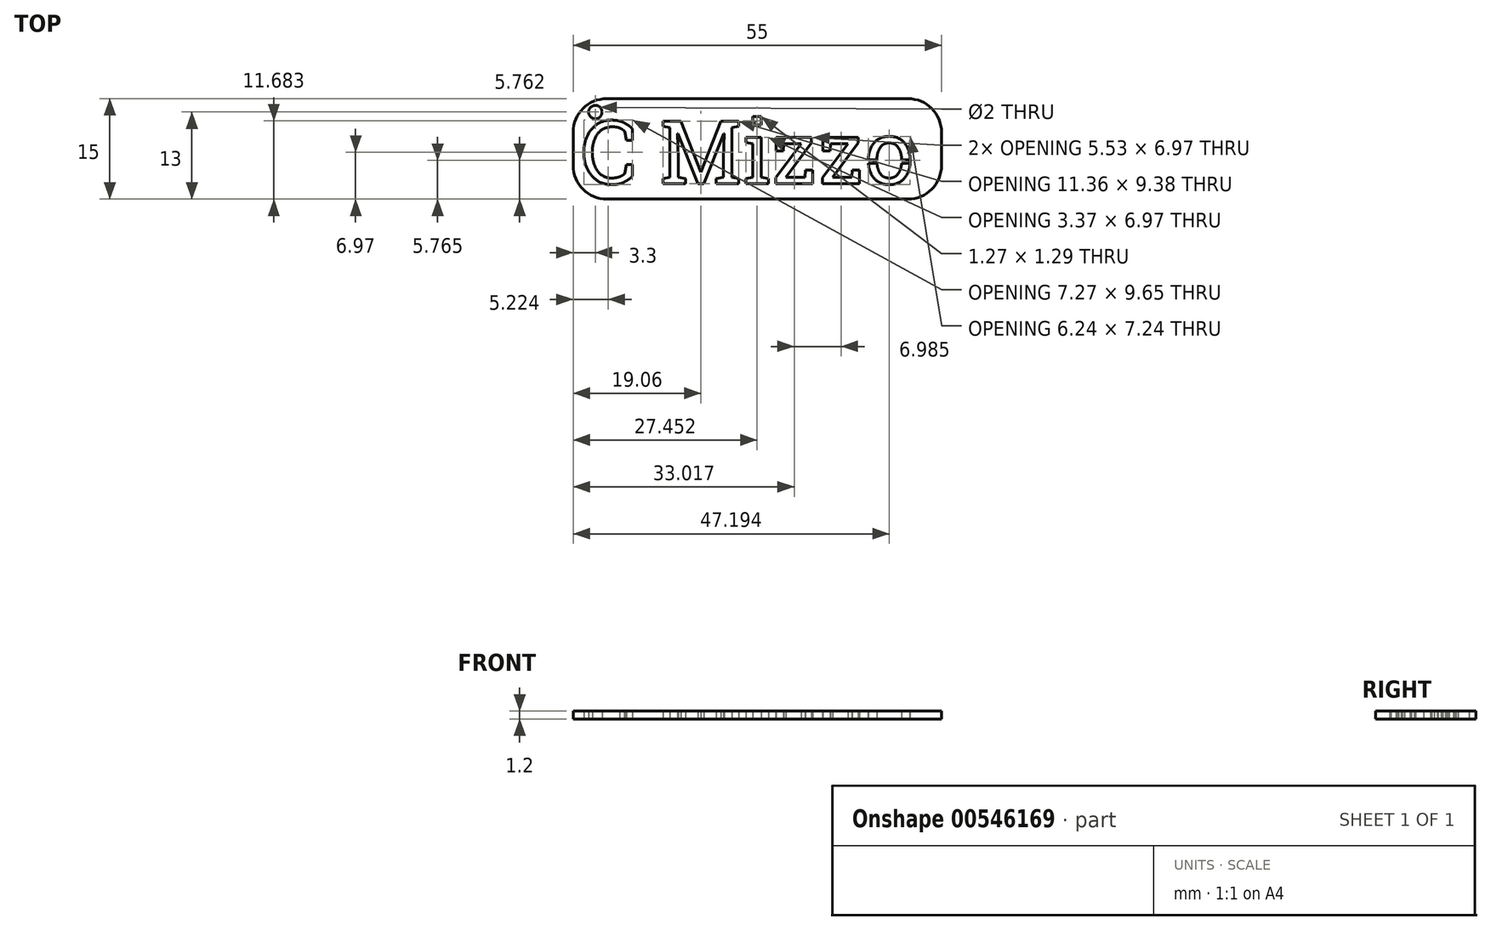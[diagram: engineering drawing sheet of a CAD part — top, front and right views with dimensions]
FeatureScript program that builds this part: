
annotation { "Feature Type Name" : "Feature", "Feature Type Description" : "" }
export const myFeature = defineFeature(function(context is Context, id is Id, definition is map)
    precondition{}
    {
        {
            var Q0;
            Q0=qCreatedBy(makeId("Top.planeOp"),FACE);
            var sketch = newSketch(context, id + "F0", { "sketchPlane" : qUnion([Q0])});
            skText(sketch, "E0", { "text": "C Mizzo", "fontName": "RobotoSlab-Regular.ttf"});
            const initialGuessF0  = {"E0": [-0.02637, -0.00522, 1, 0, 0.0095]};
            skSetInitialGuess(sketch, initialGuessF0);
            skSolve(sketch);
        }
        {
            var Q0;
            Q0=qCreatedBy(makeId("Top.planeOp"),FACE);
            var sketch = newSketch(context, id + "F1", { "sketchPlane" : qUnion([Q0])});
            skLineSegment(sketch, "E1.bottom", {"start": v(22.5, -7.5) * mm, "end": v(-22.5, -7.5) * mm});
            skLineSegment(sketch, "E1.top", {"start": v(22.5, 7.5) * mm, "end": v(-22.5, 7.5) * mm});
            skLineSegment(sketch, "E1.left", {"start": v(27.5, -2.5) * mm, "end": v(27.5, 2.5) * mm});
            skLineSegment(sketch, "E1.right", {"start": v(-27.5, -2.5) * mm, "end": v(-27.5, 2.5) * mm});
            skPoint(sketch, "E1.middle", {"position": v(0, 0) * mm});
            skPoint(sketch, "E2.visualSharp", {"position": v(-27.5, 7.5) * mm});
            skArc(sketch, "E2.filletArc", {"start": v(-22.5, 7.5) * mm, "mid": v(-26.04, 6.04) * mm, "end": v(-27.5, 2.5) * mm});
            skPoint(sketch, "E3.visualSharp", {"position": v(27.5, 7.5) * mm});
            skArc(sketch, "E3.filletArc", {"start": v(27.5, 2.5) * mm, "mid": v(26.04, 6.04) * mm, "end": v(22.5, 7.5) * mm});
            skPoint(sketch, "E4.visualSharp", {"position": v(27.5, -7.5) * mm});
            skArc(sketch, "E4.filletArc", {"start": v(22.5, -7.5) * mm, "mid": v(26.04, -6.04) * mm, "end": v(27.5, -2.5) * mm});
            skPoint(sketch, "E5.visualSharp", {"position": v(-27.5, -7.5) * mm});
            skArc(sketch, "E5.filletArc", {"start": v(-27.5, -2.5) * mm, "mid": v(-26.04, -6.04) * mm, "end": v(-22.5, -7.5) * mm});
            skSolve(sketch);
        }
        {
            var Q0;
            Q0 = qSketchRegion(id + "F1", true);
            extrude(context, id + "F2", {"entities" : qUnion([Q0]), "depth" : 1.2 * mm, "offsetDistance" : 25 * mm});
        }
        {
            var Q0;
            Q0 = qSketchRegion(id + "F0", true);
            var Q1;
            Q1=makeQuery(id+"F2.opExtrude","CAP_FACE",FACE,{"disambiguationData":[OSD([sQuery(id+"F1.wireOp",EDGE,"E1.bottom"),sQuery(id+"F1.wireOp",EDGE,"E1.top"),sQuery(id+"F1.wireOp",EDGE,"E1.left"),sQuery(id+"F1.wireOp",EDGE,"E1.right")])],"isStart":false});
            extrude(context, id + "F3", {"entities" : qUnion([Q0, Q1]), "operationType" : NewBodyOperationType.REMOVE, "depth" : 25 * mm, "offsetDistance" : 25 * mm});
        }
        {
            var Q0;
            Q0=qCreatedBy(makeId("Top.planeOp"),FACE);
            var sketch = newSketch(context, id + "F4", { "sketchPlane" : qUnion([Q0])});
            skCircle(sketch, "E6", {"center": v(-24.2, 5.5) * mm, "radius": 1 * mm});
            skSolve(sketch);
        }
        {
            var Q0;
            Q0 = qSketchRegion(id + "F4", true);
            extrude(context, id + "F5", {"entities" : qUnion([Q0]), "operationType" : NewBodyOperationType.REMOVE, "endBound" : BoundingType.THROUGH_ALL, "depth" : 25 * mm, "offsetDistance" : 25 * mm});
        }
        {
            var Q0;
            {var subQ0=sQuery(id+"F1.wireOp",EDGE,"E1.left");var subQ1=sQuery(id+"F1.wireOp",EDGE,"E1.top");var subQ2=sQuery(id+"F1.wireOp",EDGE,"E1.right");var subQ3=sQuery(id+"F1.wireOp",EDGE,"E1.bottom");var subQ4=sQuery(id+"F1.wireOp",EDGE,"E3.filletArc");var subQ5=sQuery(id+"F1.wireOp",EDGE,"E4.filletArc");var subQ6=sQuery(id+"F1.wireOp",EDGE,"E2.filletArc");var subQ7=sQuery(id+"F1.wireOp",EDGE,"E5.filletArc");Q0=makeQuery(id+"F3.boolean.opBoolean","SPLIT",FACE,{"disambiguationData":[TD([makeQuery(id+"F2.opExtrude","SWEPT_FACE",FACE,{"disambiguationData":[OSD([subQ3])]})])],"derivedFrom":makeQuery(id+"F2.opExtrude","CAP_FACE",FACE,{"disambiguationData":[OSD([subQ3,subQ1,subQ0,subQ2,subQ6,subQ4,subQ5,subQ7])],"isStart":false})});}
            var sketch = newSketch(context, id + "F6", { "sketchPlane" : qUnion([Q0])});
            skLineSegment(sketch, "E7.bottom", {"start": v(16.57, -1.63) * mm, "end": v(22.8, -1.63) * mm});
            skLineSegment(sketch, "E7.top", {"start": v(16.57, -2.13) * mm, "end": v(22.8, -2.13) * mm});
            skLineSegment(sketch, "E7.left", {"start": v(16.57, -1.63) * mm, "end": v(16.57, -2.13) * mm});
            skLineSegment(sketch, "E7.right", {"start": v(22.8, -1.63) * mm, "end": v(22.8, -2.13) * mm});
            skSolve(sketch);
        }
        {
            var Q0;
            Q0 = qSketchRegion(id + "F6", true);
            extrude(context, id + "F7", {"entities" : qUnion([Q0]), "operationType" : NewBodyOperationType.ADD, "oppositeDirection" : true, "depth" : 1.2 * mm, "offsetDistance" : 25 * mm});
        }
    });
